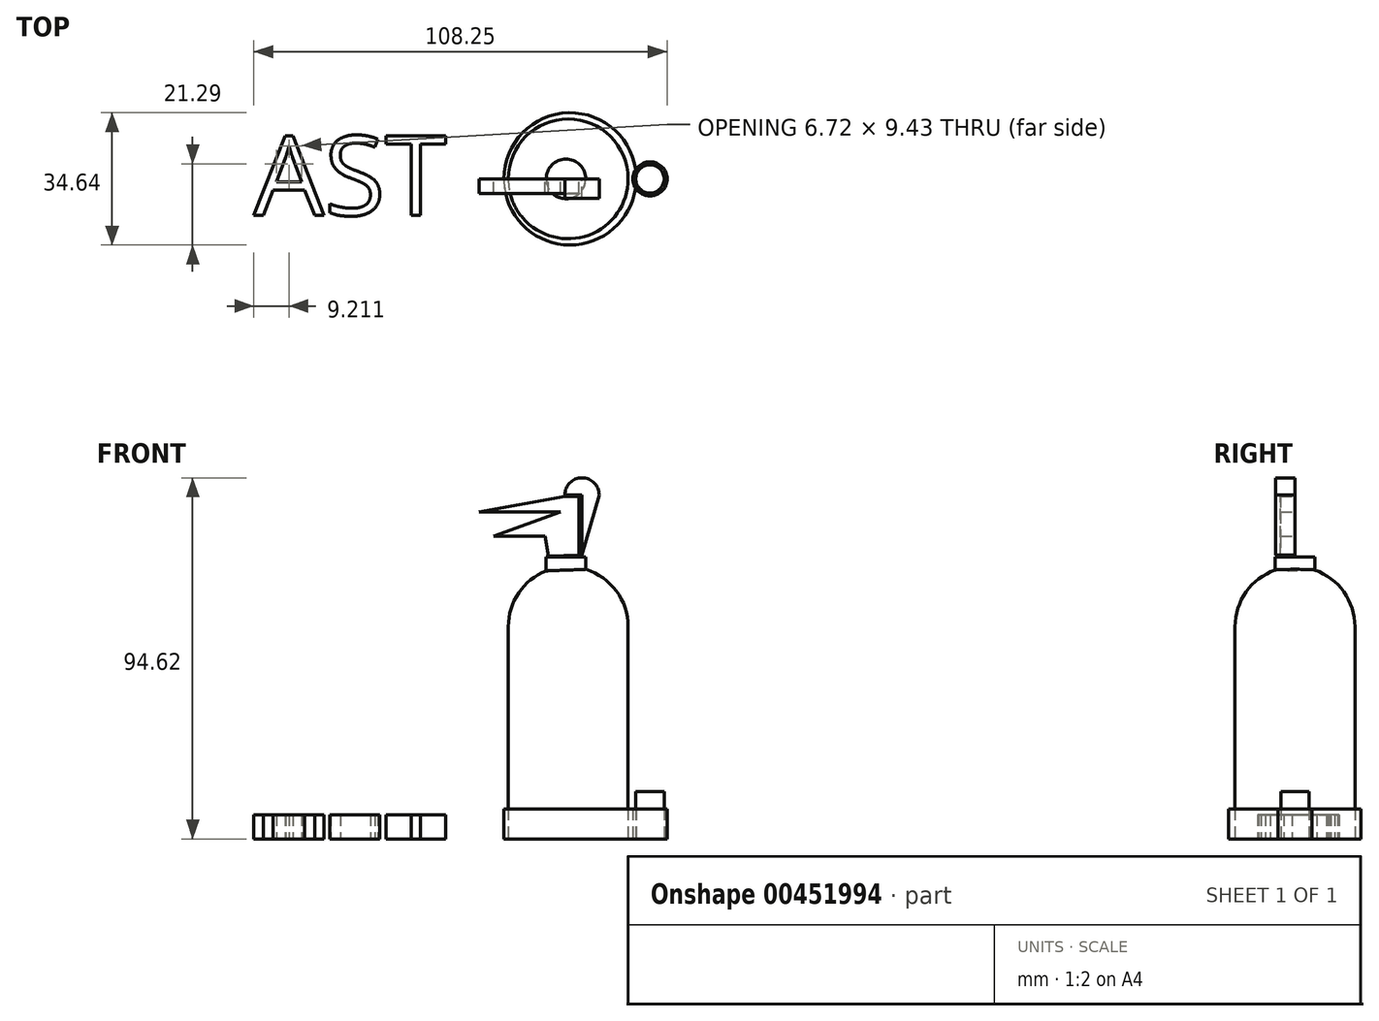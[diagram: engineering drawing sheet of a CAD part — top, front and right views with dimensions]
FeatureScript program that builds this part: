
annotation { "Feature Type Name" : "Feature", "Feature Type Description" : "" }
export const myFeature = defineFeature(function(context is Context, id is Id, definition is map)
    precondition{}
    {
        {
            var Q0;
            Q0=qCreatedBy(makeId("Top.planeOp"),FACE);
            var sketch = newSketch(context, id + "F0", { "sketchPlane" : qUnion([Q0])});
            skCircle(sketch, "E0", {"center": v(23.31, 0) * mm, "radius": 15.7 * mm});
            skSolve(sketch);
        }
        {
            var Q0;
            Q0 = qSketchRegion(id + "F0", true);
            extrude(context, id + "F1", {"entities" : qUnion([Q0]), "depth" : 55.63 * mm});
        }
        {
            var Q0;
            Q0=qCreatedBy(makeId("Front.planeOp"),FACE);
            var sketch = newSketch(context, id + "F2", { "sketchPlane" : qUnion([Q0])});
            skLineSegment(sketch, "E1.0", {"start": v(7.62, 55.63) * mm, "end": v(39, 55.63) * mm});
            skArc(sketch, "E2", {"start": v(7.62, 55.63) * mm, "mid": v(13.47, 67.85) * mm, "end": v(26.66, 70.96) * mm});
            skLineSegment(sketch, "E3", {"start": v(23.31, 55.63) * mm, "end": v(23.31, 71.32) * mm});
            skSolve(sketch);
        }
        {
            var Q0;
            {var subQ3=sQuery(id+"F2.wireOp",EDGE,"E3");Q0=makeQuery(id+"F2.imprint","IMPRINT",FACE,{"disambiguationData":[TD([[makeQuery(id+"F2.imprint","IMPRINT",EDGE,{"derivedFrom":subQ3}),1.0]])]});}
            var Q1;
            Q1=sQuery(id+"F2.wireOp",EDGE,"E3");
            revolve(context, id + "F3", {"operationType" : NewBodyOperationType.ADD, "entities" : qUnion([Q0]), "axis" : qUnion([Q1]), "revolveType" : RevolveType.FULL});
        }
        {
            var Q0;
            Q0=qCreatedBy(makeId("Top.planeOp"),FACE);
            var sketch = newSketch(context, id + "F4", { "sketchPlane" : qUnion([Q0])});
            skCircle(sketch, "E4", {"center": v(22.74, 0) * mm, "radius": 5.19 * mm});
            skSolve(sketch);
        }
        {
            var Q0;
            Q0 = qSketchRegion(id + "F4", true);
            extrude(context, id + "F5", {"entities" : qUnion([Q0]), "operationType" : NewBodyOperationType.ADD, "depth" : 73.9 * mm});
        }
        {
            var Q0;
            Q0=qCreatedBy(makeId("Front.planeOp"),FACE);
            var sketch = newSketch(context, id + "F6", { "sketchPlane" : qUnion([Q0])});
            skLineSegment(sketch, "E5", {"start": v(26.93, 74.43) * mm, "end": v(26.93, 90.13) * mm});
            skLineSegment(sketch, "E6", {"start": v(26.93, 90.13) * mm, "end": v(17.95, 90.13) * mm});
            skLineSegment(sketch, "E7", {"start": v(17.95, 90.13) * mm, "end": v(17.95, 74.05) * mm});
            skArc(sketch, "E8", {"start": v(22.44, 90.13) * mm, "mid": v(26.93, 94.62) * mm, "end": v(31.42, 90.13) * mm});
            skLineSegment(sketch, "E9", {"start": v(31.42, 90.13) * mm, "end": v(26.93, 74.43) * mm});
            skSolve(sketch);
        }
        {
            var Q0;
            Q0 = qSketchRegion(id + "F6", true);
            extrude(context, id + "F7", {"entities" : qUnion([Q0]), "depth" : 5.08 * mm});
        }
        {
            var Q0;
            Q0=qCreatedBy(makeId("Front.planeOp"),FACE);
            var sketch = newSketch(context, id + "F8", { "sketchPlane" : qUnion([Q0])});
            skLineSegment(sketch, "E10", {"start": v(26.18, 74.43) * mm, "end": v(26.18, 89.76) * mm});
            skLineSegment(sketch, "E11", {"start": v(26.18, 89.76) * mm, "end": v(22.44, 89.76) * mm});
            skLineSegment(sketch, "E12", {"start": v(22.44, 89.76) * mm, "end": v(0, 85.65) * mm});
            skLineSegment(sketch, "E13", {"start": v(0, 85.65) * mm, "end": v(21.32, 85.65) * mm});
            skLineSegment(sketch, "E14", {"start": v(21.32, 85.65) * mm, "end": v(3.74, 79.29) * mm});
            skLineSegment(sketch, "E15", {"start": v(3.74, 79.29) * mm, "end": v(17.2, 79.29) * mm});
            skLineSegment(sketch, "E16", {"start": v(17.2, 79.29) * mm, "end": v(18.16, 74.06) * mm});
            skLineSegment(sketch, "E17", {"start": v(18.16, 74.06) * mm, "end": v(26.18, 74.43) * mm});
            skSolve(sketch);
        }
        {
            var Q0;
            Q0=makeQuery(id+"F8.imprint","IMPRINT",FACE,{"disambiguationData":[TD([[makeQuery(id+"F8.imprint","IMPRINT",EDGE,{"derivedFrom":sQuery(id+"F8.wireOp",EDGE,"E10")}),1.0]])]});
            extrude(context, id + "F9", {"entities" : qUnion([Q0]), "depth" : 3.8 * mm});
        }
        {
            var Q0;
            Q0=qCreatedBy(makeId("Top.planeOp"),FACE);
            var sketch = newSketch(context, id + "F10", { "sketchPlane" : qUnion([Q0])});
            skCircle(sketch, "E18", {"center": v(44.74, 0) * mm, "radius": 3.72 * mm});
            skSolve(sketch);
        }
        {
            var Q0;
            Q0 = qSketchRegion(id + "F10", true);
            extrude(context, id + "F11", {"entities" : qUnion([Q0]), "depth" : 12.45 * mm});
        }
        {
            var Q0;
            Q0=qCreatedBy(makeId("Front.planeOp"),FACE);
            var sketch = newSketch(context, id + "F12", { "sketchPlane" : qUnion([Q0])});
            skFitSpline(sketch, "E19", {"points": [v(26.5, 75.7) * mm, v(49.5, 63.3) * mm, v(41.88, 12.85) * mm], "startDerivative": vector(70.14, -17.62) * mm, "endDerivative": vector(-33.11, -103.37) * mm});
            skFitSpline(sketch, "E20", {"points": [v(26.02, 83.79) * mm, v(54.26, 71.87) * mm, v(49.02, 11.42) * mm], "startDerivative": vector(84.7, -12.93) * mm, "endDerivative": vector(-31.59, -125.5) * mm});
            skLineSegment(sketch, "E21", {"start": v(41.88, 12.85) * mm, "end": v(49.02, 11.42) * mm});
            skLineSegment(sketch, "E22", {"start": v(26.5, 75.7) * mm, "end": v(26.02, 83.79) * mm});
            skFitSpline(sketch, "E23", {"points": [v(26.26, 79.74) * mm, v(51.3, 68.57) * mm, v(45.45, 12.14) * mm], "startDerivative": vector(75.59, -13.22) * mm, "endDerivative": vector(-30.82, -115.84) * mm});
            skSolve(sketch);
        }
        {
            var Q0;
            Q0=qCreatedBy(makeId("Top.planeOp"),FACE);
            var sketch = newSketch(context, id + "F13", { "sketchPlane" : qUnion([Q0])});
            skCircle(sketch, "E24", {"center": v(23.8, 0) * mm, "radius": 17.32 * mm});
            skSolve(sketch);
        }
        {
            var Q0;
            Q0 = qSketchRegion(id + "F13", true);
            extrude(context, id + "F14", {"entities" : qUnion([Q0]), "depth" : 7.87 * mm});
        }
        {
            var Q0;
            Q0=qCreatedBy(makeId("Top.planeOp"),FACE);
            var sketch = newSketch(context, id + "F15", { "sketchPlane" : qUnion([Q0])});
            skCircle(sketch, "E25", {"center": v(44.74, 0) * mm, "radius": 4.5 * mm});
            skSolve(sketch);
        }
        {
            var Q0;
            Q0 = qSketchRegion(id + "F15", true);
            extrude(context, id + "F16", {"entities" : qUnion([Q0]), "depth" : 7.87 * mm});
        }
        {
            var Q0;
            Q0=qCreatedBy(makeId("Top.planeOp"),FACE);
            var sketch = newSketch(context, id + "F17", { "sketchPlane" : qUnion([Q0])});
            skText(sketch, "E26", { "text": "AST\n", "fontName": "OpenSans-Regular.ttf"});
            const initialGuessF17  = {"E26": [-0.05902, -0.00952, 1, 0, 0.02094]};
            skSetInitialGuess(sketch, initialGuessF17);
            skSolve(sketch);
        }
        {
            var Q0;
            Q0 = qSketchRegion(id + "F17", true);
            extrude(context, id + "F18", {"entities" : qUnion([Q0]), "depth" : 6.35 * mm});
        }
        {
            var Q0;
            {var subQ0=sQuery(id+"F12.wireOp",EDGE,"E19");Q0=makeQuery(id+"F12.imprint","IMPRINT",FACE,{"disambiguationData":[TD([[makeQuery(id+"F12.imprint","IMPRINT",EDGE,{"derivedFrom":subQ0}),1.0]])]});}
            var Q1;
            Q1=makeQuery(id+"F11.opExtrude","CAP_EDGE",EDGE,{"disambiguationData":[OSD([sQuery(id+"F10.wireOp",EDGE,"E18")])],"isStart":false});
            var Q2;
            Q2=sQuery(id+"F12.wireOp",EDGE,"E23");
            sweep(context, id + "F19", {"bodyType" : ToolBodyType.SURFACE, "profiles" : qUnion([Q0]), "surfaceProfiles" : qUnion([Q1]), "path" : qUnion([Q2])});
        }
    });
